# Revit family: Auto-Door_Sliding_Single_Tormax_TX9500_FullBreakout_Transom_SX-SO
name_source: partatom
category: Doors
units: mm (PartAtom-declared; Revit-internal decimal feet)

## family parameters
Always vertical = Yes
Classification Number = 23.30.10.17.11
Cut with Voids When Loaded = No
Host = Wall
Room Calculation Point = No
Shared = No

## types (3) — shared parameters
Analytic Construction = <None>
Assembly Code = B2030110
Available Options = [Standard Weatherstripping][Electric Lock][Battery Backup][Door Position Monitoring][I/O Module][Key Switch]
CAD Details = https://www.arcat.com
Construction Details = http://www.arcat.com
Define Thermal Properties by = Schematic Type
Fire Rating = as Specified
Frame Thickness = 0' - 4 1/2"
Glazing Thickness_Fixed Panel = 0' - 0 1/2"
Glazing Thickness_Sliding Panel = 0' - 0 1/2"
Green Building-LEED = http://www.arcat.com
HD Drive = No
Has Partial Breakout Capability = Yes
Height = 10' - 11"
Keynote = 08 71 13
Manufacturer = Tormax
Max Height = 0' - 0"
Max Width = 0' - 0"
Miami Dade Conformance = Does Not Apply
Model = TX9500
Operating Temperature Range = Ambient -30F to 130F
Panel Thickness = 0' - 1 3/4"
Product Data = http://www.arcat.com
Product Page URL = https://www.arcat.com
RO Spacing_Sides = 0' - 0 1/4"
RO Spacing_Top = 0' - 0 1/4"
Sales Information = http://www.tormaxusa.com
Specification = https://www.arcat.com
Standards Conformance = ANSI A156.10  ;  NFPA 101  ;  UL325  ;  C-UL
Thickness = 0' - 1 3/4"
Transom Height = 3' - 4"
Type Comments = Transom XO
URL = http://www.tormaxusa.com
Wall Closure = By host
Water Penetration = as Specified
headerdepth = 0' - 8"
zero-valued in all types: Expected Lifespan (Years), Maintenance Schedule (Months), Warranty Duration (Years)

## per-type parameters (varying)
| type | Description | Unit Width |
| 7'-0" Package Width | Single RH Inside Slide Application w/Transom (SX-SO), Full Breakout, 7'-0" Package Width | 7' - 0" |
| 8'-0" Package Width | Single RH Inside Slide Application w/Transom (SX-SO), Full Breakout, 8'-0" Package Width | 8' - 0" |
| 9'-0" Package Width | Single RH Inside Slide Application w/Transom (SX-SO), Full Breakout, 9'-0" Package Width | 9' - 0" |

## geometry (parser evidence)
native form markers: Sweep x8
no freeform markers — native parametric forms only
